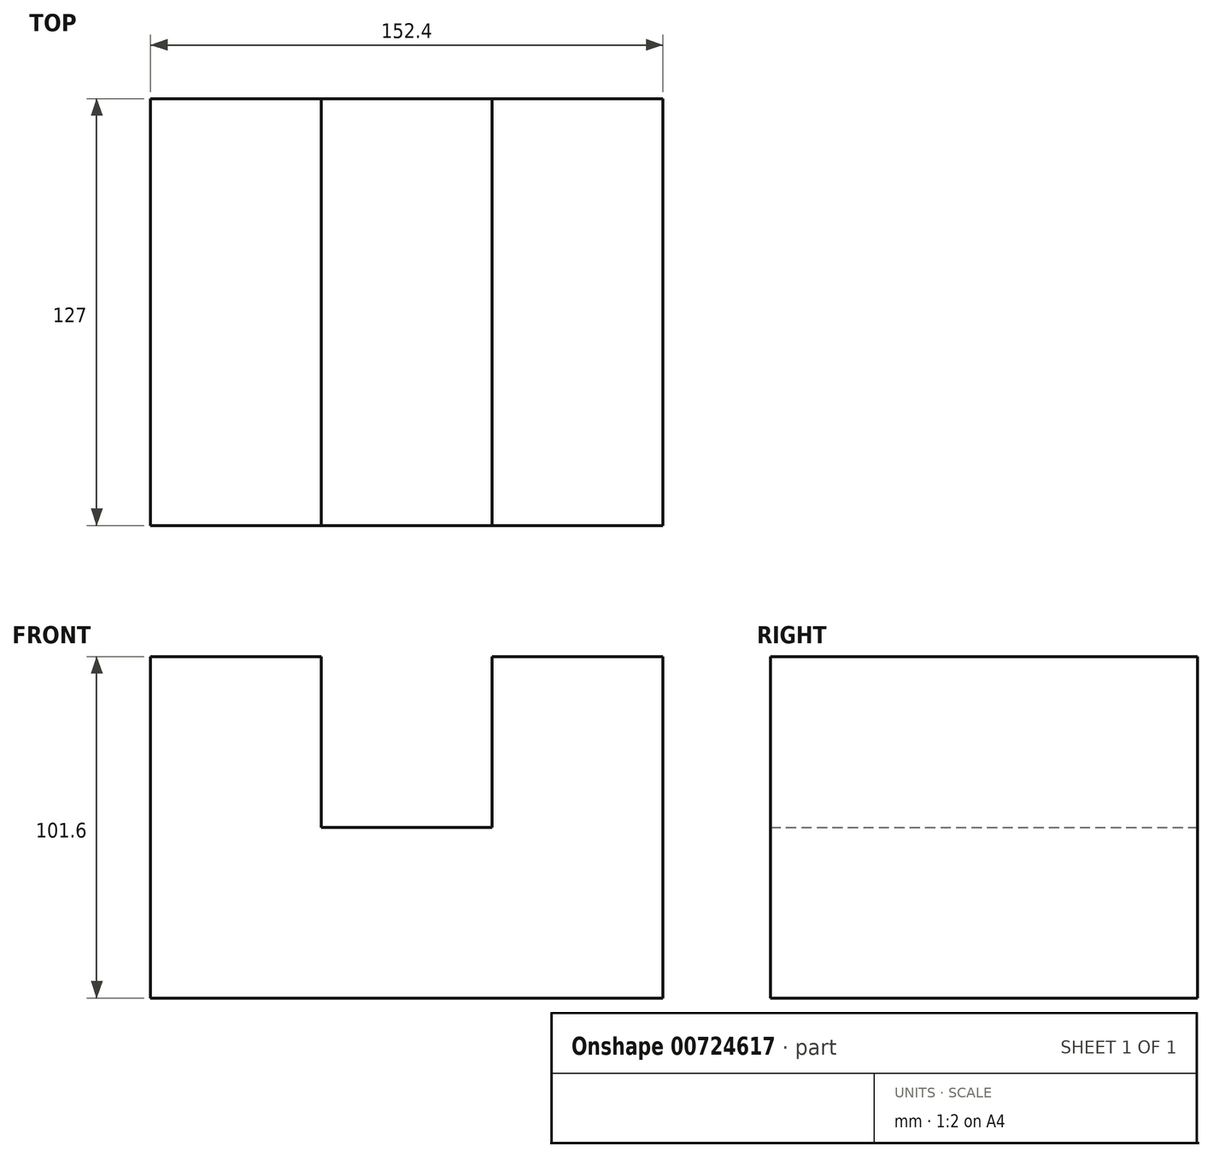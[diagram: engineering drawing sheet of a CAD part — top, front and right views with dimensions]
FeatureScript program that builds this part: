
annotation { "Feature Type Name" : "Feature", "Feature Type Description" : "" }
export const myFeature = defineFeature(function(context is Context, id is Id, definition is map)
    precondition{}
    {
        {
            var Q0;
            Q0=qCreatedBy(makeId("Front.planeOp"),FACE);
            var sketch = newSketch(context, id + "F0", { "sketchPlane" : qUnion([Q0])});
            skLineSegment(sketch, "E0", {"start": v(-71.81, -50.8) * mm, "end": v(-71.81, 50.8) * mm});
            skLineSegment(sketch, "E1", {"start": v(-71.81, -50.8) * mm, "end": v(80.59, -50.8) * mm});
            skLineSegment(sketch, "E2", {"start": v(80.59, -50.8) * mm, "end": v(80.59, 50.8) * mm});
            skLineSegment(sketch, "E3", {"start": v(-71.81, 50.8) * mm, "end": v(-21.01, 50.8) * mm});
            skLineSegment(sketch, "E4", {"start": v(-21.01, 50.8) * mm, "end": v(-21.01, 0) * mm});
            skLineSegment(sketch, "E5", {"start": v(-21.01, 0) * mm, "end": v(29.79, 0) * mm});
            skLineSegment(sketch, "E6", {"start": v(29.79, 0) * mm, "end": v(29.79, 50.8) * mm});
            skLineSegment(sketch, "E7", {"start": v(29.79, 50.8) * mm, "end": v(80.59, 50.8) * mm});
            skSolve(sketch);
        }
        {
            var Q0;
            Q0 = qSketchRegion(id + "F0", true);
            extrude(context, id + "F1", {"entities" : qUnion([Q0]), "depth" : 127 * mm, "offsetDistance" : 25.4 * mm});
        }
    });
